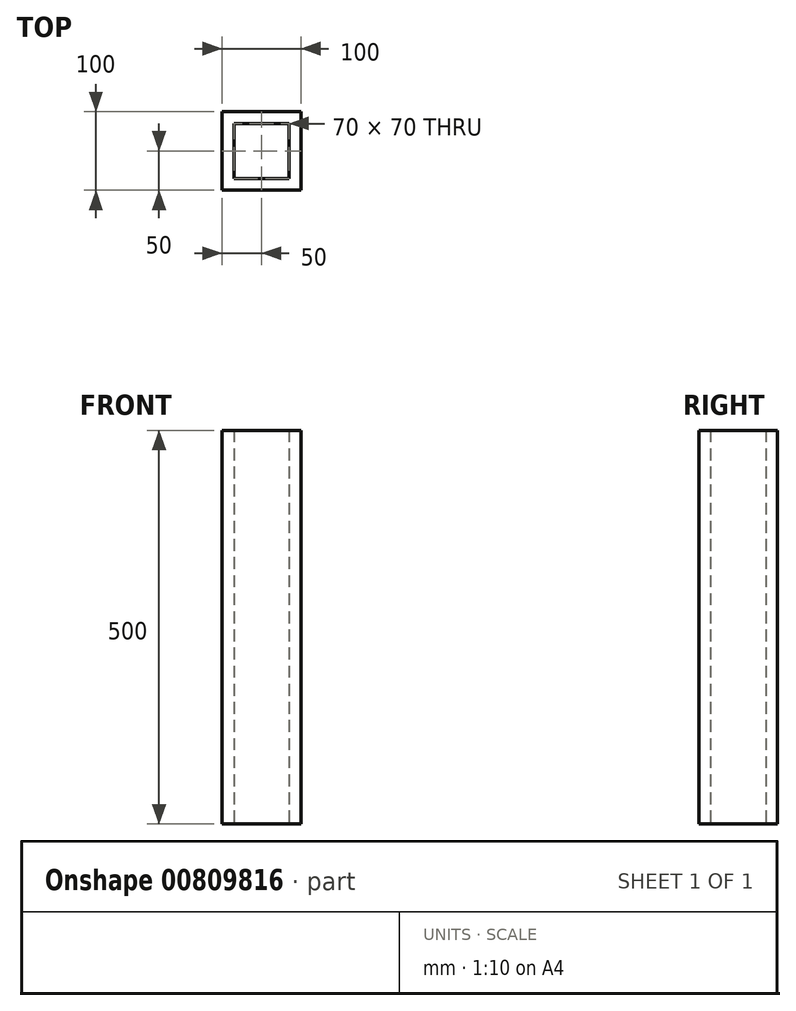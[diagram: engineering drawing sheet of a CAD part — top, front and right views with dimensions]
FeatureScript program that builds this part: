
annotation { "Feature Type Name" : "Feature", "Feature Type Description" : "" }
export const myFeature = defineFeature(function(context is Context, id is Id, definition is map)
    precondition{}
    {
        {
            var Q0;
            Q0=qCreatedBy(makeId("Top.planeOp"),FACE);
            var sketch = newSketch(context, id + "F0", { "sketchPlane" : qUnion([Q0])});
            skLineSegment(sketch, "E0.bottom", {"start": v(-50, 50) * mm, "end": v(50, 50) * mm});
            skLineSegment(sketch, "E0.top", {"start": v(-50, -50) * mm, "end": v(50, -50) * mm});
            skLineSegment(sketch, "E0.left", {"start": v(-50, 50) * mm, "end": v(-50, -50) * mm});
            skLineSegment(sketch, "E0.right", {"start": v(50, 50) * mm, "end": v(50, -50) * mm});
            skLineSegment(sketch, "E1.bottom", {"start": v(-35, 35) * mm, "end": v(35, 35) * mm});
            skLineSegment(sketch, "E1.top", {"start": v(-35, -35) * mm, "end": v(35, -35) * mm});
            skLineSegment(sketch, "E1.left", {"start": v(-35, 35) * mm, "end": v(-35, -35) * mm});
            skLineSegment(sketch, "E1.right", {"start": v(35, 35) * mm, "end": v(35, -35) * mm});
            skSolve(sketch);
        }
        {
            var Q0;
            Q0=makeQuery(id+"F0.imprint","IMPRINT",FACE,{"disambiguationData":[TD([[makeQuery(id+"F0.imprint","IMPRINT",EDGE,{"derivedFrom":sQuery(id+"F0.wireOp",EDGE,"E0.bottom")}),-1.0]])]});
            extrude(context, id + "F1", {"entities" : qUnion([Q0]), "depth" : 500 * mm, "offsetDistance" : 25 * mm});
        }
    });
